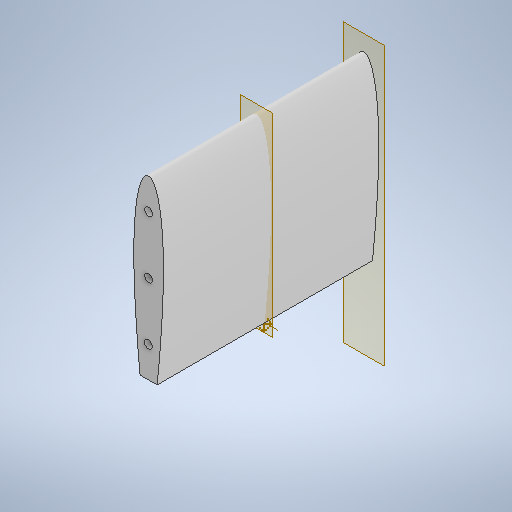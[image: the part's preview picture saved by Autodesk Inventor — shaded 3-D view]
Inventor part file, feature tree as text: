
AUTODESK INVENTOR PART (.ipt)
format: ipt  version: 2025.2 (Build 292293000, 293)  size: 289,280 bytes
history: native  units: in
note: dims shown in document units (in); Inventor stores cm internally (conversion verified against a paired STEP export)
features: other x7, plane x2, extrude x2, sketch x2, mirror x1
ambient origin geometry x8: Origin, YZ Plane, XZ Plane, XY Plane, X Axis, Y Axis, Z Axis, Center Point
bodies: Solid1 (feature_tree)
feature tree (14):
  plane  "Work Plane1"
  extrude  "Extrusion1"  Depth=6.9929in TaperAngle=0.0deg
  extrude  "Extrusion2"  Depth=1.0in
  other  "Work Point2"
  other  "Work Axis1"
  plane  "Work Plane2"
  mirror  "Mirror1"
  sketch  "Sketch1"  dims[d4=5.7346in d5=6.9929in d6=0.0in]
  sketch  "Sketch2"  dims[d8=0.25in d10=0.25in d12=0.25in d22=1.0in d25=1.8675in d26=1.0in d27=0.0in d28=1.0in d29=1.8671in]
  other  "Work Point1"
  other  "Work Point3"
  other  "<userpath>\OneDrive\Documents\Spring 2025\Senior Design\Tail\TailAssembly.iam"
  other  "TailAssembly.iam"
  other  "InnerTailLeft"
